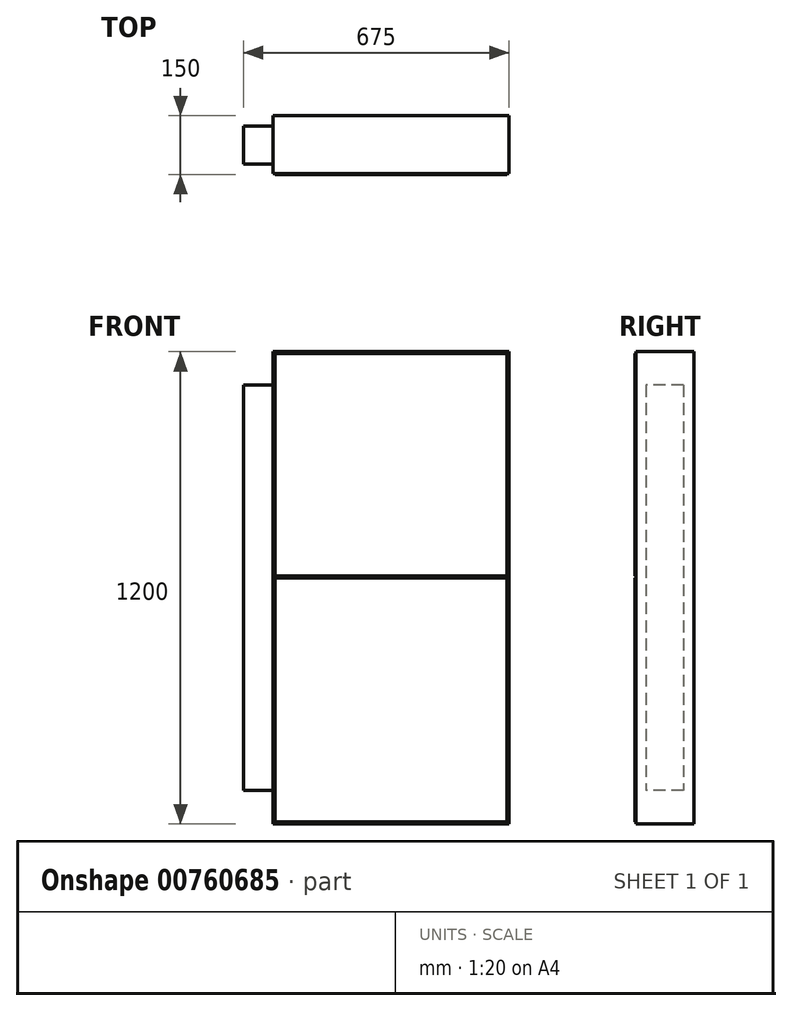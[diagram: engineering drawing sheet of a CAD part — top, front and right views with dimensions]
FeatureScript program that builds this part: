
annotation { "Feature Type Name" : "Feature", "Feature Type Description" : "" }
export const myFeature = defineFeature(function(context is Context, id is Id, definition is map)
    precondition{}
    {
        {
            var Q0;
            Q0=qCreatedBy(makeId("Front.planeOp"),FACE);
            var sketch = newSketch(context, id + "F0", { "sketchPlane" : qUnion([Q0])});
            skLineSegment(sketch, "E0.bottom", {"start": v(-846.92, 1133.82) * mm, "end": v(-246.92, 1133.82) * mm});
            skLineSegment(sketch, "E0.top", {"start": v(-846.92, -66.18) * mm, "end": v(-246.92, -66.18) * mm});
            skLineSegment(sketch, "E0.left", {"start": v(-846.92, 1133.82) * mm, "end": v(-846.92, -66.18) * mm});
            skLineSegment(sketch, "E0.right", {"start": v(-246.92, 1133.82) * mm, "end": v(-246.92, -66.18) * mm});
            skSolve(sketch);
        }
        {
            var Q0;
            Q0 = qSketchRegion(id + "F0", true);
            extrude(context, id + "F1", {"entities" : qUnion([Q0]), "depth" : 150 * mm, "offsetDistance" : 25 * mm, "symmetric" : true});
        }
        {
            var Q0;
            Q0=makeQuery(id+"F1.opExtrude","CAP_FACE",FACE,{"disambiguationData":[OSD([sQuery(id+"F0.wireOp",EDGE,"E0.bottom"),sQuery(id+"F0.wireOp",EDGE,"E0.top"),sQuery(id+"F0.wireOp",EDGE,"E0.left"),sQuery(id+"F0.wireOp",EDGE,"E0.right")])],"isStart":false});
            var sketch = newSketch(context, id + "F2", { "sketchPlane" : qUnion([Q0])});
            skLineSegment(sketch, "E1.0", {"start": v(-841.92, 1128.82) * mm, "end": v(-841.92, 563.82) * mm});
            skLineSegment(sketch, "E1.1", {"start": v(-841.92, 1128.82) * mm, "end": v(-251.92, 1128.82) * mm});
            skLineSegment(sketch, "E1.2", {"start": v(-251.92, 1128.82) * mm, "end": v(-251.92, 563.82) * mm});
            skLineSegment(sketch, "E1.3", {"start": v(-841.92, -61.18) * mm, "end": v(-251.92, -61.18) * mm});
            skLineSegment(sketch, "E2", {"start": v(-841.92, 563.82) * mm, "end": v(-251.92, 563.82) * mm});
            skLineSegment(sketch, "E3.0", {"start": v(-841.92, 558.82) * mm, "end": v(-251.92, 558.82) * mm});
            skLineSegment(sketch, "E4.0", {"start": v(-846.92, 1133.82) * mm, "end": v(-846.92, -66.18) * mm});
            skLineSegment(sketch, "E4.1", {"start": v(-246.92, 1133.82) * mm, "end": v(-246.92, -66.18) * mm});
            skLineSegment(sketch, "E4.2", {"start": v(-846.92, 1133.82) * mm, "end": v(-246.92, 1133.82) * mm});
            skLineSegment(sketch, "E5", {"start": v(-846.92, -66.18) * mm, "end": v(-246.92, -66.18) * mm});
            skLineSegment(sketch, "E6.trimOffspring", {"start": v(-841.92, 558.82) * mm, "end": v(-841.92, -61.18) * mm});
            skLineSegment(sketch, "E7.trimOffspring", {"start": v(-251.92, 558.82) * mm, "end": v(-251.92, -61.18) * mm});
            skSolve(sketch);
        }
        {
            var Q0;
            Q0=makeQuery(id+"F2.imprint","IMPRINT",FACE,{"disambiguationData":[TD([[makeQuery(id+"F2.imprint","IMPRINT",EDGE,{"derivedFrom":sQuery(id+"F2.wireOp",EDGE,"E1.0")}),-1.0]])]});
            extrude(context, id + "F3", {"entities" : qUnion([Q0]), "operationType" : NewBodyOperationType.REMOVE, "oppositeDirection" : true, "depth" : 2 * mm, "offsetDistance" : 25 * mm});
        }
        {
            var Q0;
            Q0=makeQuery(id+"F1.opExtrude","SWEPT_FACE",FACE,{"disambiguationData":[OSD([sQuery(id+"F0.wireOp",EDGE,"E0.left")])]});
            var sketch = newSketch(context, id + "F4", { "sketchPlane" : qUnion([Q0])});
            skLineSegment(sketch, "E8.bottom", {"start": v(-48, 1048.82) * mm, "end": v(48, 1048.82) * mm});
            skLineSegment(sketch, "E8.top", {"start": v(-48, 18.82) * mm, "end": v(48, 18.82) * mm});
            skLineSegment(sketch, "E8.left", {"start": v(-48, 1048.82) * mm, "end": v(-48, 18.82) * mm});
            skLineSegment(sketch, "E8.right", {"start": v(48, 1048.82) * mm, "end": v(48, 18.82) * mm});
            skSolve(sketch);
        }
        {
            var Q0;
            Q0 = qSketchRegion(id + "F4", true);
            extrude(context, id + "F5", {"entities" : qUnion([Q0]), "operationType" : NewBodyOperationType.ADD, "depth" : 75 * mm, "offsetDistance" : 25 * mm});
        }
    });
